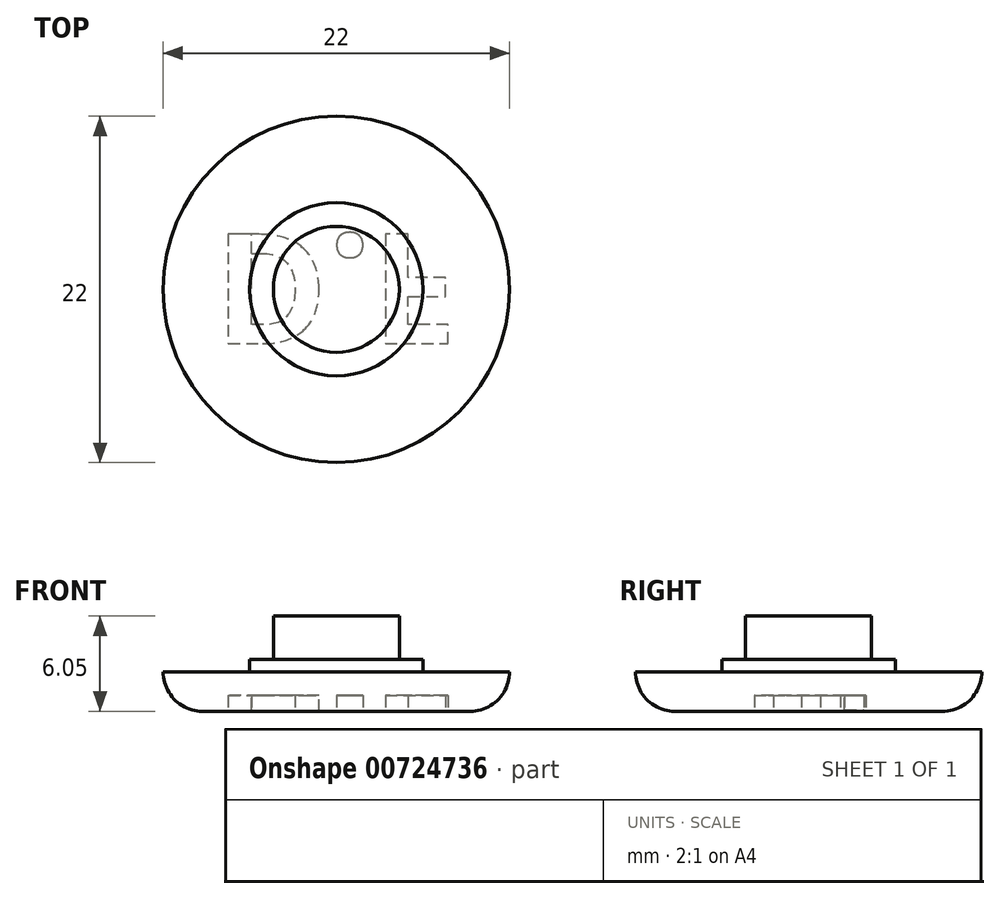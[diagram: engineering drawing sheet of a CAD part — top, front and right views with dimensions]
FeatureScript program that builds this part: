
annotation { "Feature Type Name" : "Feature", "Feature Type Description" : "" }
export const myFeature = defineFeature(function(context is Context, id is Id, definition is map)
    precondition{}
    {
        {
            var Q0;
            Q0=qCreatedBy(makeId("Top.planeOp"),FACE);
            var sketch = newSketch(context, id + "F0", { "sketchPlane" : qUnion([Q0])});
            skCircle(sketch, "E0", {"center": v(0, 0) * mm, "radius": 11 * mm});
            skCircle(sketch, "E1", {"center": v(0, 0) * mm, "radius": 4 * mm});
            skCircle(sketch, "E2", {"center": v(0, 0) * mm, "radius": 5.5 * mm});
            skSolve(sketch);
        }
        {
            var Q0;
            Q0=makeQuery(id+"F0.imprint","IMPRINT",FACE,{"disambiguationData":[TD([[makeQuery(id+"F0.imprint","IMPRINT",EDGE,{"derivedFrom":sQuery(id+"F0.wireOp",EDGE,"E0")}),1.0]])]});
            extrude(context, id + "F1", {"entities" : qUnion([Q0]), "depth" : 2.5 * mm, "offsetDistance" : 25 * mm});
        }
        {
            var Q0;
            Q0=makeQuery(id+"F0.imprint","IMPRINT",FACE,{"disambiguationData":[TD([[makeQuery(id+"F0.imprint","IMPRINT",EDGE,{"derivedFrom":sQuery(id+"F0.wireOp",EDGE,"E1")}),-1.0]])]});
            var Q1;
            Q1=makeQuery(id+"F1.opExtrude","CAP_FACE",FACE,{"disambiguationData":[OSD([sQuery(id+"F0.wireOp",EDGE,"E0"),sQuery(id+"F0.wireOp",EDGE,"E2")])],"isStart":false});
            extrude(context, id + "F2", {"entities" : qUnion([Q0]), "operationType" : NewBodyOperationType.ADD, "endBound" : BoundingType.UP_TO_SURFACE, "depth" : 25 * mm, "endBoundEntityFace" : qUnion([Q1]), "hasOffset" : true, "offsetDistance" : .8 * mm, "offsetOppositeDirection" : true});
        }
        {
            var Q0;
            Q0=makeQuery(id+"F0.imprint","IMPRINT",FACE,{"disambiguationData":[TD([[makeQuery(id+"F0.imprint","IMPRINT",EDGE,{"derivedFrom":sQuery(id+"F0.wireOp",EDGE,"E1")}),1.0]])]});
            var Q1;
            Q1=makeQuery(id+"F2.opExtrude","CAP_FACE",FACE,{"disambiguationData":[OSD([sQuery(id+"F0.wireOp",EDGE,"E0"),sQuery(id+"F0.wireOp",EDGE,"E2")])],"isStart":false});
            extrude(context, id + "F3", {"entities" : qUnion([Q0]), "operationType" : NewBodyOperationType.ADD, "endBound" : BoundingType.UP_TO_SURFACE, "depth" : 3 * mm, "endBoundEntityFace" : qUnion([Q1]), "hasOffset" : true, "offsetDistance" : 2.75 * mm, "offsetOppositeDirection" : true});
        }
        {
            var Q0;
            {var subQ0=sQuery(id+"F0.wireOp",EDGE,"E1");var subQ1=sQuery(id+"F0.wireOp",EDGE,"E2");Q0=makeQuery(id+"F3.boolean.opBoolean","MERGE",FACE,{"derivedFrom":[makeQuery(id+"F2.boolean.opBoolean","MERGE",FACE,{"derivedFrom":[makeQuery(id+"F1.opExtrude","CAP_FACE",FACE,{"disambiguationData":[OSD([sQuery(id+"F0.wireOp",EDGE,"E0"),subQ1])],"isStart":true}),makeQuery(id+"F2.opExtrude","CAP_FACE",FACE,{"disambiguationData":[OSD([subQ0,subQ1])],"isStart":true})]}),makeQuery(id+"F3.opExtrude","CAP_FACE",FACE,{"disambiguationData":[OSD([subQ0])],"isStart":true})]});}
            fillet(context, id + "F4", {"entities" : qUnion([Q0]), "radius" : 2.5 * mm, "tangentPropagation" : true, "allowEdgeOverflow" : false});
        }
        {
            var Q0;
            Q0=qCreatedBy(makeId("Right.planeOp"),FACE);
            var sketch = newSketch(context, id + "F5", { "sketchPlane" : qUnion([Q0])});
            skEllipse(sketch, "E3", {"center": v(-63.43, -1.89) * mm, "majorRadius": 11 * mm, "minorRadius": 2.5 * mm, "majorAxis": v(-1, 0)});
            skPoint(sketch, "E4", {"position": v(-63.43, 0.61) * mm});
            skLineSegment(sketch, "E5", {"start": v(-55.79, 0) * mm, "end": v(-71.08, 0) * mm});
            skArc(sketch, "E6", {"start": v(-11, 2.37) * mm, "mid": v(-6, 2.57) * mm, "end": v(-11, 2.5) * mm});
            skArc(sketch, "E7", {"start": v(6, 2.5) * mm, "mid": v(6, 2.46) * mm, "end": v(6, 2.42) * mm});
            skLineSegment(sketch, "E8", {"start": v(-63.43, 0.61) * mm, "end": v(-63.43, -4.39) * mm});
            skPoint(sketch, "E9.orphan", {"position": v(-63.43, -3.78) * mm});
            skPoint(sketch, "E10.orphan", {"position": v(-63.43, 0) * mm});
            skSolve(sketch);
        }
        {
            var Q0;
            {var subQ0=sQuery(id+"F0.wireOp",EDGE,"E1");var subQ1=sQuery(id+"F0.wireOp",EDGE,"E2");Q0=makeQuery(id+"F3.boolean.opBoolean","MERGE",FACE,{"derivedFrom":[makeQuery(id+"F2.boolean.opBoolean","MERGE",FACE,{"derivedFrom":[makeQuery(id+"F1.opExtrude","CAP_FACE",FACE,{"disambiguationData":[OSD([sQuery(id+"F0.wireOp",EDGE,"E0"),subQ1])],"isStart":true}),makeQuery(id+"F2.opExtrude","CAP_FACE",FACE,{"disambiguationData":[OSD([subQ0,subQ1])],"isStart":true})]}),makeQuery(id+"F3.opExtrude","CAP_FACE",FACE,{"disambiguationData":[OSD([subQ0])],"isStart":true})]});}
            var sketch = newSketch(context, id + "F6", { "sketchPlane" : qUnion([Q0])});
            skSolve(sketch);
        }
        {
            var Q0;
            {var subQ0=sQuery(id+"F0.wireOp",EDGE,"E1");var subQ1=sQuery(id+"F0.wireOp",EDGE,"E2");var subQ2=sQuery(id+"F0.wireOp",EDGE,"E0");Q0=makeQuery(id+"F6.imprint","IMPRINT",FACE,{"disambiguationData":[TD([[makeQuery(id+"F6.imprint","IMPRINT",EDGE,{"derivedFrom":makeQuery(id+"F4.opFillet","BLEND_EDGE",EDGE,{"blendedFrom":[makeQuery(id+"F1.opExtrude","CAP_EDGE",EDGE,{"disambiguationData":[OSD([subQ2])],"isStart":true}),makeQuery(id+"F3.boolean.opBoolean","MERGE",FACE,{"derivedFrom":[makeQuery(id+"F2.boolean.opBoolean","MERGE",FACE,{"derivedFrom":[makeQuery(id+"F1.opExtrude","CAP_FACE",FACE,{"disambiguationData":[OSD([subQ2,subQ1])],"isStart":true}),makeQuery(id+"F2.opExtrude","CAP_FACE",FACE,{"disambiguationData":[OSD([subQ0,subQ1])],"isStart":true})]}),makeQuery(id+"F3.opExtrude","CAP_FACE",FACE,{"disambiguationData":[OSD([subQ0])],"isStart":true})]})],"blendedInto":[makeQuery(id+"F3.boolean.opBoolean","MERGE",FACE,{"derivedFrom":[makeQuery(id+"F2.boolean.opBoolean","MERGE",FACE,{"derivedFrom":[makeQuery(id+"F1.opExtrude","CAP_FACE",FACE,{"disambiguationData":[OSD([subQ2,subQ1])],"isStart":true}),makeQuery(id+"F2.opExtrude","CAP_FACE",FACE,{"disambiguationData":[OSD([subQ0,subQ1])],"isStart":true})]}),makeQuery(id+"F3.opExtrude","CAP_FACE",FACE,{"disambiguationData":[OSD([subQ0])],"isStart":true})]})]})}),1.0]])]});}
            var sketch = newSketch(context, id + "F7", { "sketchPlane" : qUnion([Q0])});
            skLineSegment(sketch, "E11", {"start": v(-8.5, 0) * mm, "end": v(8.5, 0) * mm});
            skText(sketch, "E12", { "text": "D.F", "fontName": "OpenSans-Bold.ttf"});
            const initialGuessF7  = {"E12": [-0.00774, -0.0035, 1, 0, 0.00701]};
            skSetInitialGuess(sketch, initialGuessF7);
            skSolve(sketch);
        }
        {
            var Q0;
            Q0=qSketchRegion(id+"F7",true);
            extrude(context, id + "F8", {"entities" : qUnion([Q0]), "operationType" : NewBodyOperationType.REMOVE, "oppositeDirection" : true, "depth" : 1 * mm, "offsetDistance" : 25 * mm});
        }
        {
            var Q0;
            {var subQ0=sQuery(id+"F0.wireOp",EDGE,"E1");var subQ1=sQuery(id+"F0.wireOp",EDGE,"E2");var subQ2=sQuery(id+"F0.wireOp",EDGE,"E0");Q0=makeQuery(id+"F6.imprint","IMPRINT",FACE,{"disambiguationData":[TD([[makeQuery(id+"F6.imprint","IMPRINT",EDGE,{"derivedFrom":makeQuery(id+"F4.opFillet","BLEND_EDGE",EDGE,{"blendedFrom":[makeQuery(id+"F1.opExtrude","CAP_EDGE",EDGE,{"disambiguationData":[OSD([subQ2])],"isStart":true}),makeQuery(id+"F3.boolean.opBoolean","MERGE",FACE,{"derivedFrom":[makeQuery(id+"F2.boolean.opBoolean","MERGE",FACE,{"derivedFrom":[makeQuery(id+"F1.opExtrude","CAP_FACE",FACE,{"disambiguationData":[OSD([subQ2,subQ1])],"isStart":true}),makeQuery(id+"F2.opExtrude","CAP_FACE",FACE,{"disambiguationData":[OSD([subQ0,subQ1])],"isStart":true})]}),makeQuery(id+"F3.opExtrude","CAP_FACE",FACE,{"disambiguationData":[OSD([subQ0])],"isStart":true})]})],"blendedInto":[makeQuery(id+"F3.boolean.opBoolean","MERGE",FACE,{"derivedFrom":[makeQuery(id+"F2.boolean.opBoolean","MERGE",FACE,{"derivedFrom":[makeQuery(id+"F1.opExtrude","CAP_FACE",FACE,{"disambiguationData":[OSD([subQ2,subQ1])],"isStart":true}),makeQuery(id+"F2.opExtrude","CAP_FACE",FACE,{"disambiguationData":[OSD([subQ0,subQ1])],"isStart":true})]}),makeQuery(id+"F3.opExtrude","CAP_FACE",FACE,{"disambiguationData":[OSD([subQ0])],"isStart":true})]})]})}),1.0]])]});}
            var sketch = newSketch(context, id + "F9", { "sketchPlane" : qUnion([Q0])});
            skLineSegment(sketch, "E13", {"start": v(-5.4, -2.28) * mm, "end": v(-5.4, -3.5) * mm});
            skLineSegment(sketch, "E14", {"start": v(-5.38, -2.28) * mm, "end": v(-5.38, -3.5) * mm});
            skLineSegment(sketch, "E15", {"start": v(-5.38, -3.5) * mm, "end": v(-5.4, -3.5) * mm});
            skLineSegment(sketch, "E16", {"start": v(-5.4, -2.28) * mm, "end": v(-5.38, -2.28) * mm});
            skSolve(sketch);
        }
        {
            var Q0;
            Q0 = qSketchRegion(id + "F9", true);
            extrude(context, id + "F10", {"entities" : qUnion([Q0]), "operationType" : NewBodyOperationType.ADD, "oppositeDirection" : true, "depth" : .1 * mm, "offsetDistance" : 25 * mm});
        }
    });
